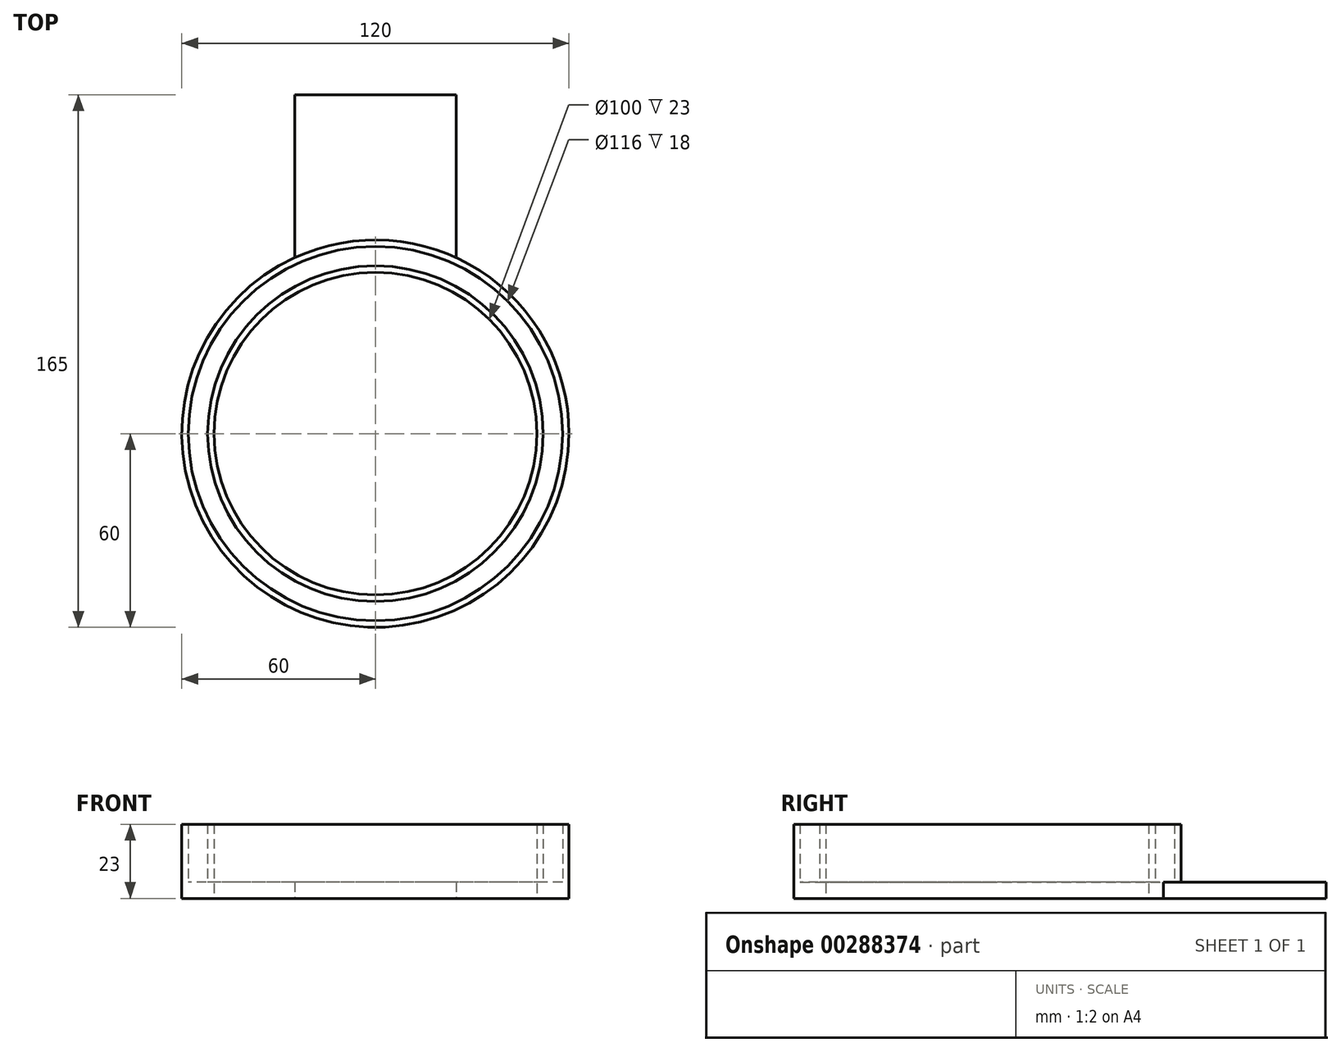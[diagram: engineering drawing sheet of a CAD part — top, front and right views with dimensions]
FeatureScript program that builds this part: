
annotation { "Feature Type Name" : "Feature", "Feature Type Description" : "" }
export const myFeature = defineFeature(function(context is Context, id is Id, definition is map)
    precondition{}
    {
        {
            var Q0;
            Q0=qCreatedBy(makeId("Top.planeOp"),FACE);
            var sketch = newSketch(context, id + "F0", { "sketchPlane" : qUnion([Q0])});
            skCircle(sketch, "E0", {"center": v(0, 0) * mm, "radius": 50 * mm});
            skCircle(sketch, "E1", {"center": v(0, 0) * mm, "radius": 60 * mm});
            skLineSegment(sketch, "E2", {"start": v(0, 0) * mm, "end": v(0, 121.73) * mm, "construction": true});
            skLineSegment(sketch, "E3", {"start": v(25, 60) * mm, "end": v(25, 105) * mm});
            skLineSegment(sketch, "E4", {"start": v(25, 105) * mm, "end": v(-25, 105) * mm});
            skLineSegment(sketch, "E5", {"start": v(-25, 105) * mm, "end": v(-25, 54.54) * mm});
            skLineSegment(sketch, "E6", {"start": v(25, 60) * mm, "end": v(25, 54.54) * mm});
            skSolve(sketch);
        }
        {
            var Q0;
            Q0 = qSketchRegion(id + "F0", true);
            extrude(context, id + "F1", {"entities" : qUnion([Q0]), "depth" : 5 * mm, "offsetDistance" : 25 * mm});
        }
        {
            var Q0;
            Q0=makeQuery(id+"F1.opExtrude","CAP_FACE",FACE,{"disambiguationData":[OSD([sQuery(id+"F0.wireOp",EDGE,"E0"),sQuery(id+"F0.wireOp",EDGE,"E1")])],"isStart":false});
            var sketch = newSketch(context, id + "F2", { "sketchPlane" : qUnion([Q0])});
            skCircle(sketch, "E7", {"center": v(0, 0) * mm, "radius": 52 * mm});
            skCircle(sketch, "E8", {"center": v(0, 0) * mm, "radius": 58 * mm});
            skCircle(sketch, "E9", {"center": v(0, 0) * mm, "radius": 60 * mm});
            skSolve(sketch);
        }
        {
            var Q0;
            Q0=makeQuery(id+"F2.imprint","IMPRINT",FACE,{"disambiguationData":[TD([[makeQuery(id+"F2.imprint","IMPRINT",EDGE,{"derivedFrom":sQuery(id+"F2.wireOp",EDGE,"E8")}),-1.0]])]});
            var Q1;
            Q1=makeQuery(id+"F2.imprint","IMPRINT",FACE,{"disambiguationData":[TD([[makeQuery(id+"F2.imprint","IMPRINT",EDGE,{"derivedFrom":sQuery(id+"F2.wireOp",EDGE,"E7")}),1.0]])]});
            extrude(context, id + "F3", {"entities" : qUnion([Q0, Q1]), "operationType" : NewBodyOperationType.ADD, "depth" : 18 * mm, "offsetDistance" : 25 * mm});
        }
    });
